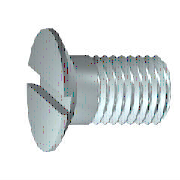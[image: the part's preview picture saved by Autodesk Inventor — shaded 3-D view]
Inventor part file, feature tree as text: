
AUTODESK INVENTOR PART (.ipt)
format: ipt  version: 2017 (Build 210142000, 142)  size: 172,544 bytes
history: native  units: mm (DEFAULTED — no unit token found)
features: sketch x2, extrude x1, plane x1
ambient origin geometry x7: Origin, YZ Plane, XZ Plane, X Axis, Y Axis, Z Axis, Center Point
bodies: Solid1 (feature_tree), Body (feature_tree)
feature tree (4):
  extrude  "Slot"  Depth=8.0mm
  plane  "Work Plane1"
  sketch  "Sketch1"  dims[d0=8.0mm d1=45.0deg d2=0.24538mm d3=6.0mm d4=1.2mm d5=1.50924mm]
  sketch  "Sketch2"  dims[d6=2.0mm d7=3.5mm d19=90.0deg d8=0.4mm d9=0.0mm d10=6.0mm d11=0.0mm d12=0.24538mm d13=0.12269mm d15=0.7mm d16=3.5mm d17=0.0mm d35=45.0deg d39=0.0mm d40=0.0mm]
